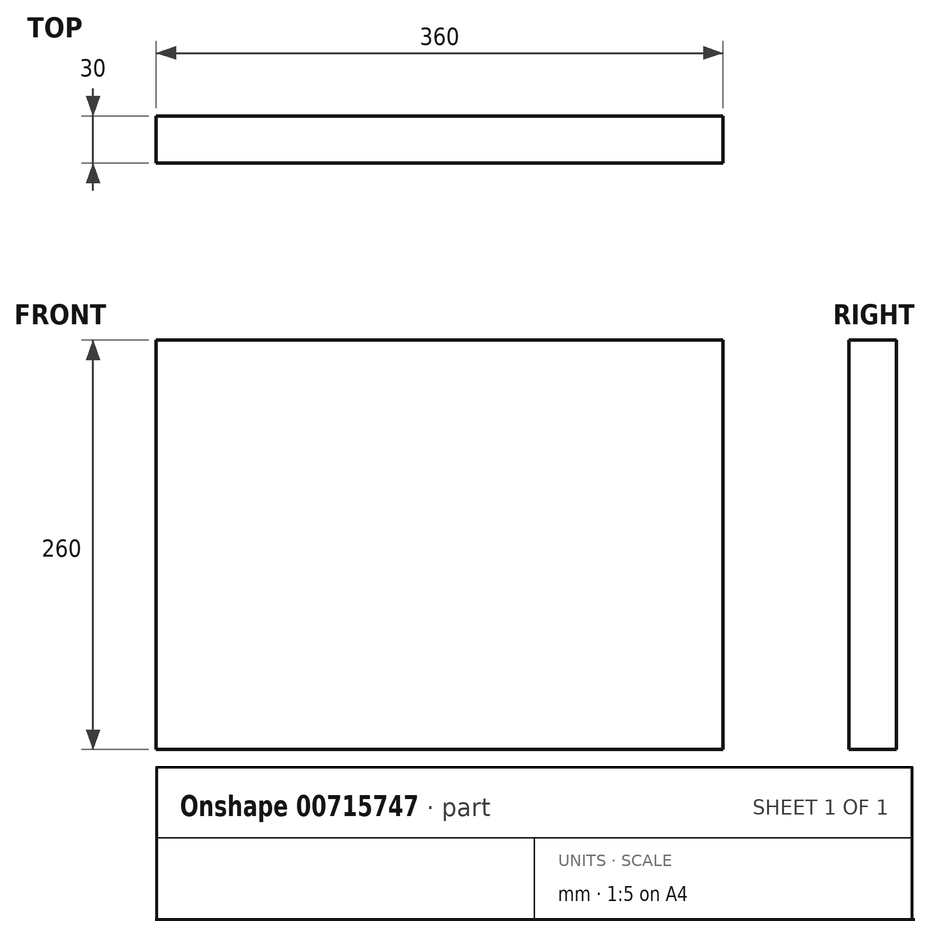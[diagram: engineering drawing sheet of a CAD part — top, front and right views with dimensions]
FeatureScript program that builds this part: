
annotation { "Feature Type Name" : "Feature", "Feature Type Description" : "" }
export const myFeature = defineFeature(function(context is Context, id is Id, definition is map)
    precondition{}
    {
        {
            var Q0;
            Q0=qCreatedBy(makeId("Front.planeOp"),FACE);
            var sketch = newSketch(context, id + "F0", { "sketchPlane" : qUnion([Q0])});
            skLineSegment(sketch, "E0.bottom", {"start": v(-180, 130) * mm, "end": v(180, 130) * mm});
            skLineSegment(sketch, "E0.top", {"start": v(-180, -130) * mm, "end": v(180, -130) * mm});
            skLineSegment(sketch, "E0.left", {"start": v(-180, 130) * mm, "end": v(-180, -130) * mm});
            skLineSegment(sketch, "E0.right", {"start": v(180, 130) * mm, "end": v(180, -130) * mm});
            skSolve(sketch);
        }
        {
            var Q0;
            Q0=qSketchRegion(id+"F0",true);
            extrude(context, id + "F1", {"entities" : qUnion([Q0]), "depth" : 30 * mm, "offsetDistance" : 25 * mm});
        }
    });
